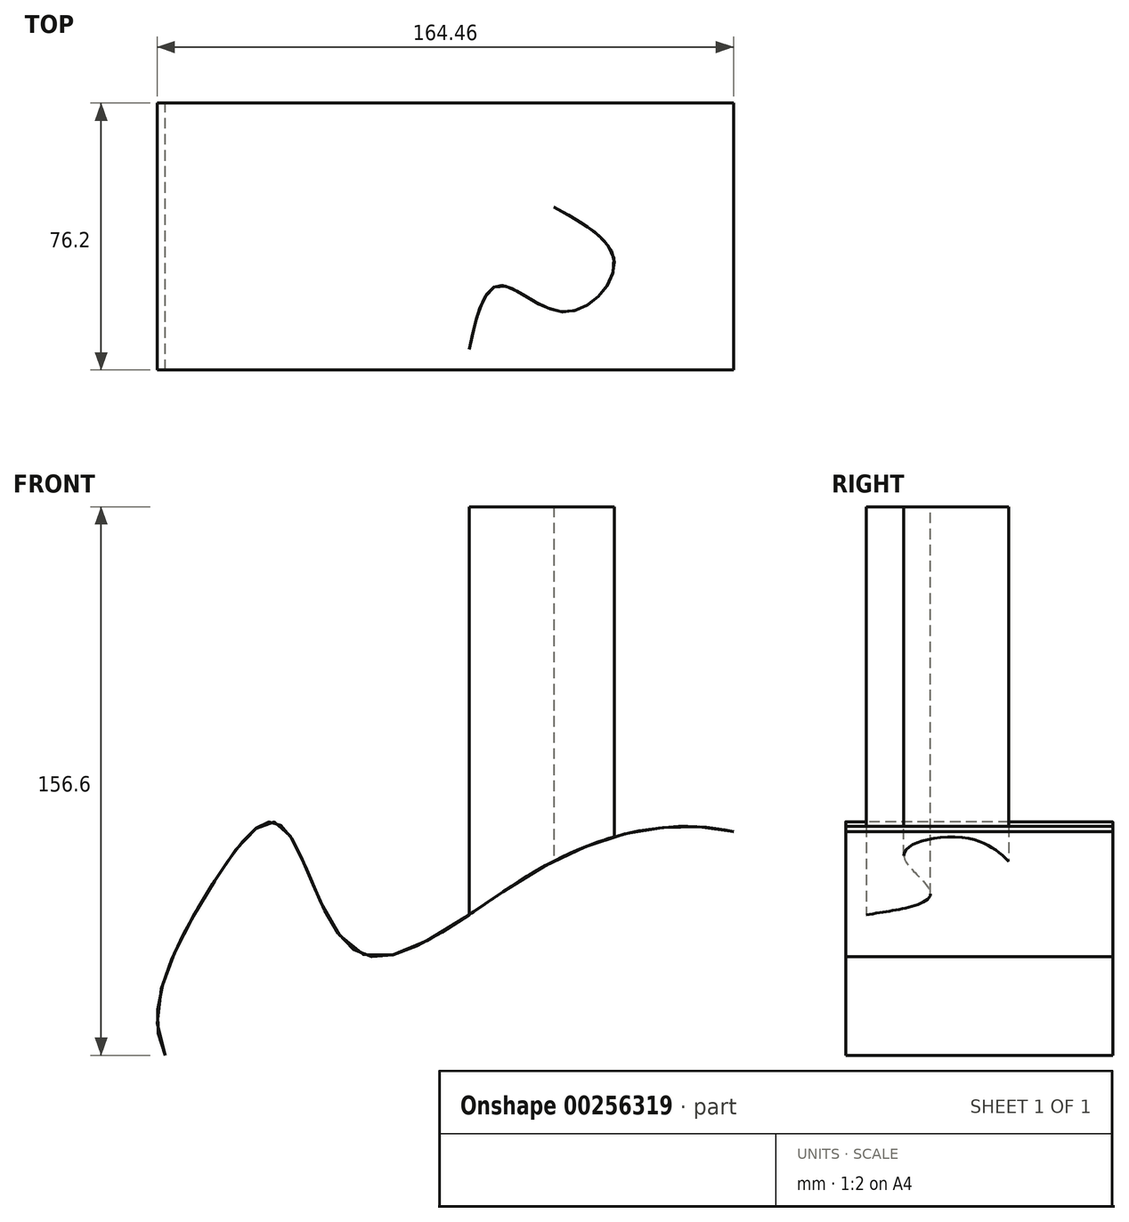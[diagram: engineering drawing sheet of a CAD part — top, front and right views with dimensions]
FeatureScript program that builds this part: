
annotation { "Feature Type Name" : "Feature", "Feature Type Description" : "" }
export const myFeature = defineFeature(function(context is Context, id is Id, definition is map)
    precondition{}
    {
        {
            var Q0;
            Q0=qCreatedBy(makeId("Front.planeOp"),FACE);
            var sketch = newSketch(context, id + "F0", { "sketchPlane" : qUnion([Q0])});
            skFitSpline(sketch, "E0", {"points": [v(-117.59, -29.6) * mm, v(-104.95, 17.84) * mm, v(-85, 36.36) * mm, v(-62.98, 0) * mm, v(-10.04, 24.03) * mm, v(44.52, 34.26) * mm], "startDerivative": vector(-101.2, 196.41) * mm, "endDerivative": vector(218.77, -48.81) * mm});
            skSolve(sketch);
        }
        {
            var Q0;
            Q0=sQuery(id+"F0.wireOp",EDGE,"E0");
            extrude(context, id + "F1", {"bodyType" : ToolBodyType.SURFACE, "surfaceEntities" : qUnion([Q0]), "oppositeDirection" : true, "depth" : 76.2 * mm});
        }
        {
            var Q0;
            Q0=qCreatedBy(makeId("Top.planeOp"),FACE);
            cPlane(context, id + "F2", {"entities" : qUnion([Q0]), "cplaneType" : CPlaneType.OFFSET, "offset" : 127 * mm, "width" : 152.4 * mm, "height" : 152.4 * mm});
        }
        {
            var Q0;
            Q0=qCreatedBy(id+"F2.planeOp",FACE);
            var sketch = newSketch(context, id + "F3", { "sketchPlane" : qUnion([Q0])});
            skFitSpline(sketch, "E1", {"points": [v(-6.81, 46.55) * mm, v(10.54, 30.48) * mm, v(-3.53, 16.6) * mm, v(-22.44, 24.17) * mm, v(-30.92, 5.9) * mm], "startDerivative": vector(97.55, -52.97) * mm, "endDerivative": vector(-24.1, -108.93) * mm});
            skSolve(sketch);
        }
        {
            var Q0;
            Q0=sQuery(id+"F3.wireOp",EDGE,"E1");
            var Q1;
            Q1=makeQuery(id+"F1.opExtrude","SWEPT_FACE",FACE,{"disambiguationData":[OSD([sQuery(id+"F0.wireOp",EDGE,"E0")])]});
            extrude(context, id + "F4", {"bodyType" : ToolBodyType.SURFACE, "surfaceEntities" : qUnion([Q0]), "endBound" : BoundingType.UP_TO_SURFACE, "oppositeDirection" : true, "endBoundEntityFace" : qUnion([Q1]), "depth" : 25.4 * mm});
        }
    });
